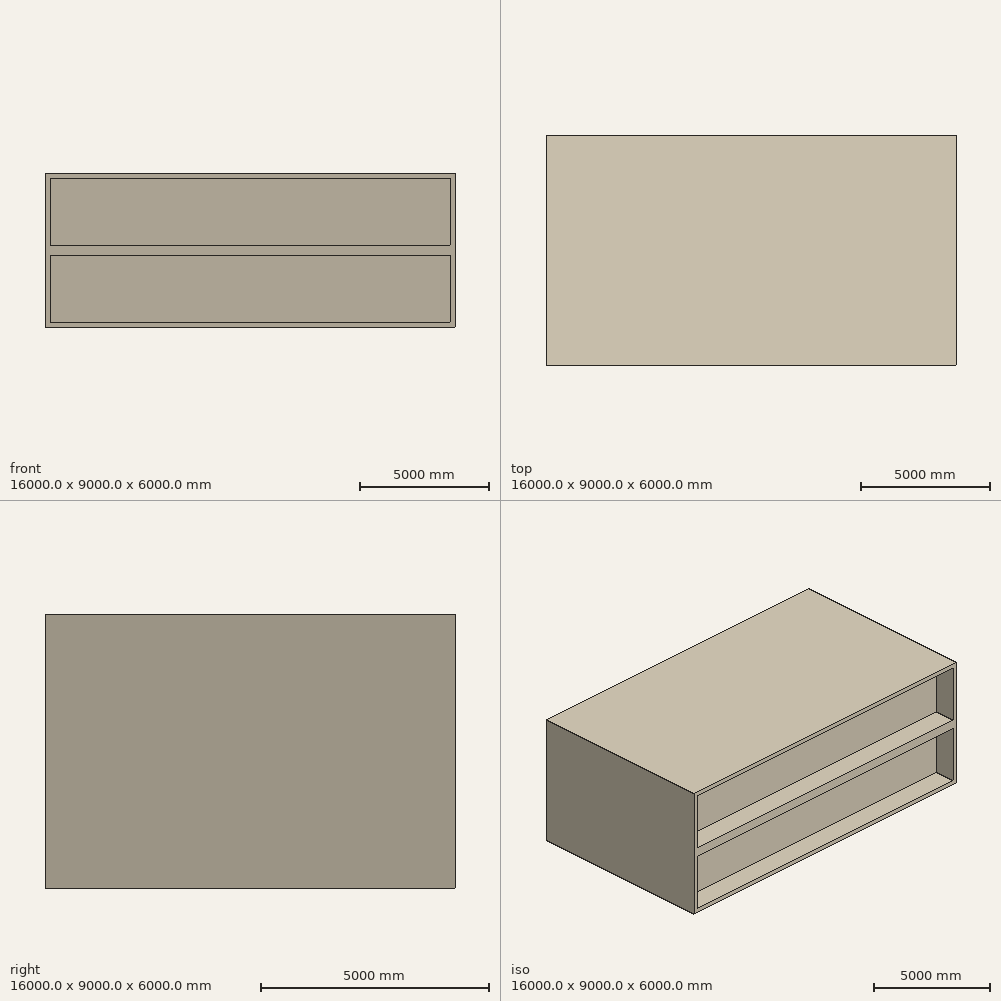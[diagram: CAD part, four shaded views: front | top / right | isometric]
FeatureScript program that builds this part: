
annotation { "Feature Type Name" : "Feature", "Feature Type Description" : "" }
export const myFeature = defineFeature(function(context is Context, id is Id, definition is map)
    precondition{}
    {
        {
            var Q0;
            Q0=qCreatedBy(makeId("Front.planeOp"),FACE);
            var sketch = newSketch(context, id + "F0", { "sketchPlane" : qUnion([Q0])});
            skLineSegment(sketch, "E0.bottom", {"start": v(-8000, -3000) * mm, "end": v(8000, -3000) * mm});
            skLineSegment(sketch, "E0.top", {"start": v(-8000, 3000) * mm, "end": v(8000, 3000) * mm});
            skLineSegment(sketch, "E0.left", {"start": v(-8000, -3000) * mm, "end": v(-8000, 3000) * mm});
            skLineSegment(sketch, "E0.right", {"start": v(8000, -3000) * mm, "end": v(8000, 3000) * mm});
            skPoint(sketch, "E0.middle", {"position": v(0, 0) * mm});
            skSolve(sketch);
        }
        {
            var Q0;
            Q0=makeQuery(id+"F0.imprint","IMPRINT",FACE,{"disambiguationData":[TD([[makeQuery(id+"F0.imprint","IMPRINT",EDGE,{"derivedFrom":sQuery(id+"F0.wireOp",EDGE,"E0.bottom")}),1.0]])]});
            extrude(context, id + "F1", {"entities" : qUnion([Q0]), "depth" : 9000 * mm, "offsetDistance" : 25 * mm});
        }
        {
            var Q0;
            Q0=makeQuery(id+"F1.opExtrude","CAP_FACE",FACE,{"disambiguationData":[OSD([sQuery(id+"F0.wireOp",EDGE,"E0.bottom"),sQuery(id+"F0.wireOp",EDGE,"E0.top"),sQuery(id+"F0.wireOp",EDGE,"E0.left"),sQuery(id+"F0.wireOp",EDGE,"E0.right")])],"isStart":false});
            var sketch = newSketch(context, id + "F2", { "sketchPlane" : qUnion([Q0])});
            skLineSegment(sketch, "E1.bottom", {"start": v(7800, -2800) * mm, "end": v(-7800, -2800) * mm});
            skLineSegment(sketch, "E1.top", {"start": v(7800, 2800) * mm, "end": v(-7800, 2800) * mm});
            skLineSegment(sketch, "E1.left", {"start": v(7800, -2800) * mm, "end": v(7800, 2800) * mm});
            skLineSegment(sketch, "E1.right", {"start": v(-7800, -2800) * mm, "end": v(-7800, 2800) * mm});
            skPoint(sketch, "E1.middle", {"position": v(0, 0) * mm});
            skSolve(sketch);
        }
        {
            var Q0;
            Q0=makeQuery(id+"F2.imprint","IMPRINT",FACE,{"disambiguationData":[TD([[makeQuery(id+"F2.imprint","IMPRINT",EDGE,{"derivedFrom":sQuery(id+"F2.wireOp",EDGE,"E1.bottom")}),-1.0]])]});
            extrude(context, id + "F3", {"entities" : qUnion([Q0]), "operationType" : NewBodyOperationType.REMOVE, "depth" : -1000 * mm, "offsetDistance" : 25 * mm});
        }
        {
            var Q0;
            Q0=makeQuery(id+"F3.boolean.opBoolean","COPY",FACE,{"derivedFrom":makeQuery(id+"F3.opExtrude","CAP_FACE",FACE,{"disambiguationData":[OSD([sQuery(id+"F2.wireOp",EDGE,"E1.bottom"),sQuery(id+"F2.wireOp",EDGE,"E1.top"),sQuery(id+"F2.wireOp",EDGE,"E1.left"),sQuery(id+"F2.wireOp",EDGE,"E1.right")])],"isStart":false})});
            var sketch = newSketch(context, id + "F4", { "sketchPlane" : qUnion([Q0])});
            skLineSegment(sketch, "E2.bottom", {"start": v(7800, -210.64) * mm, "end": v(-7800, -210.64) * mm});
            skLineSegment(sketch, "E2.top", {"start": v(7800, 210.64) * mm, "end": v(-7800, 210.64) * mm});
            skLineSegment(sketch, "E2.left", {"start": v(7800, -210.64) * mm, "end": v(7800, 210.64) * mm});
            skLineSegment(sketch, "E2.right", {"start": v(-7800, -210.64) * mm, "end": v(-7800, 210.64) * mm});
            skPoint(sketch, "E2.middle", {"position": v(0, 0) * mm});
            skSolve(sketch);
        }
        {
            var Q0;
            Q0=makeQuery(id+"F4.imprint","IMPRINT",FACE,{"disambiguationData":[TD([[makeQuery(id+"F4.imprint","IMPRINT",EDGE,{"derivedFrom":sQuery(id+"F4.wireOp",EDGE,"E2.bottom")}),-1.0]])]});
            extrude(context, id + "F5", {"entities" : qUnion([Q0]), "operationType" : NewBodyOperationType.ADD, "depth" : 1000 * mm, "offsetDistance" : 25 * mm});
        }
    });
